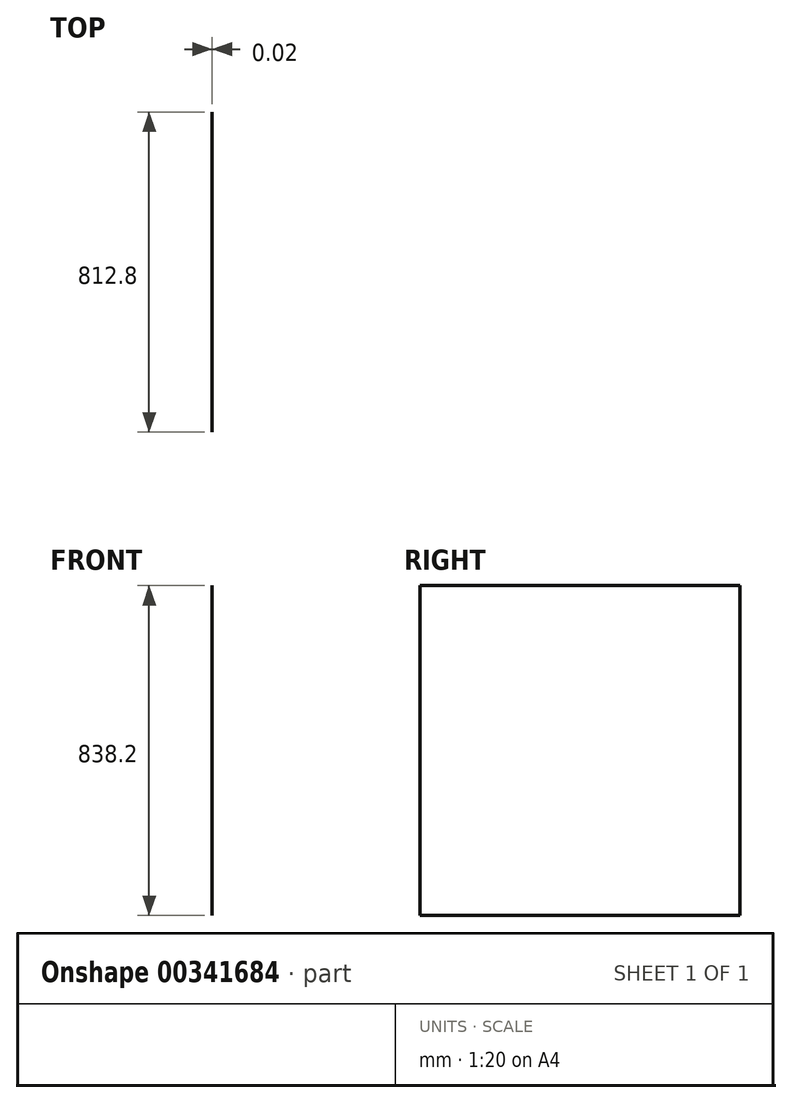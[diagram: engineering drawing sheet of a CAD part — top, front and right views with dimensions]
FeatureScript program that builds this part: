
annotation { "Feature Type Name" : "Feature", "Feature Type Description" : "" }
export const myFeature = defineFeature(function(context is Context, id is Id, definition is map)
    precondition{}
    {
        {
            var Q0;
            Q0=qCreatedBy(makeId("Right.planeOp"),FACE);
            var sketch = newSketch(context, id + "F0", { "sketchPlane" : qUnion([Q0])});
            skLineSegment(sketch, "E0.bottom", {"start": v(-403.52, 499.96) * mm, "end": v(409.28, 499.96) * mm});
            skLineSegment(sketch, "E0.top", {"start": v(-403.52, -338.24) * mm, "end": v(409.28, -338.24) * mm});
            skLineSegment(sketch, "E0.left", {"start": v(-403.52, 499.96) * mm, "end": v(-403.52, -338.24) * mm});
            skLineSegment(sketch, "E0.right", {"start": v(409.28, 499.96) * mm, "end": v(409.28, -338.24) * mm});
            skSolve(sketch);
        }
        {
            var Q0;
            Q0=makeQuery(id+"F0.imprint","IMPRINT",FACE,{"disambiguationData":[TD([[makeQuery(id+"F0.imprint","IMPRINT",EDGE,{"derivedFrom":sQuery(id+"F0.wireOp",EDGE,"E0.bottom")}),-1.0]])]});
            extrude(context, id + "F1", {"entities" : qUnion([Q0]), "depth" : 1 / 50.8 * mm});
        }
    });
